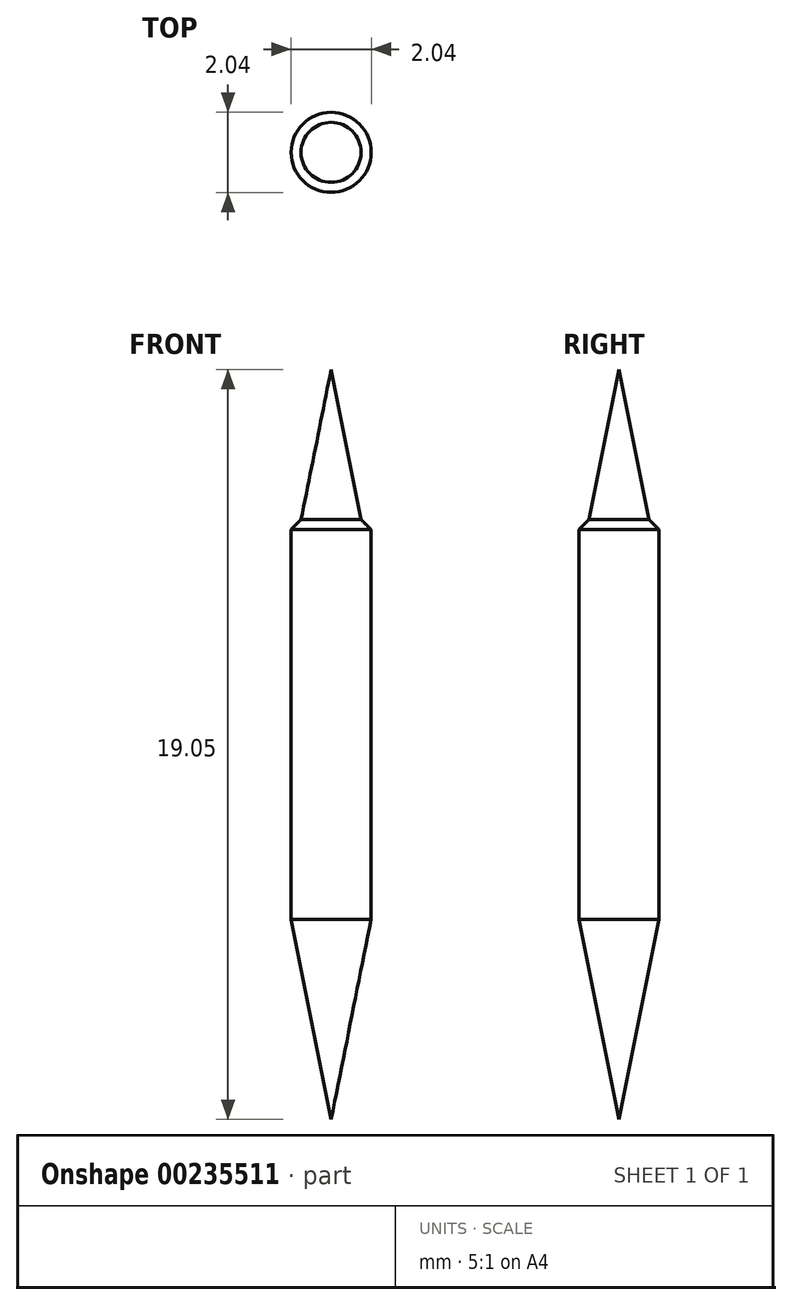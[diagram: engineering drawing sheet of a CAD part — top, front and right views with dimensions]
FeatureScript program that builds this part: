
annotation { "Feature Type Name" : "Feature", "Feature Type Description" : "" }
export const myFeature = defineFeature(function(context is Context, id is Id, definition is map)
    precondition{}
    {
        {
            var Q0;
            Q0=qCreatedBy(makeId("Front.planeOp"),FACE);
            var sketch = newSketch(context, id + "F0", { "sketchPlane" : qUnion([Q0])});
            skLineSegment(sketch, "E0", {"start": v(-1.02, 9.9) * mm, "end": v(-1.02, 0) * mm});
            skLineSegment(sketch, "E1", {"start": v(-1.02, 0) * mm, "end": v(1.02, 0) * mm});
            skLineSegment(sketch, "E2", {"start": v(1.02, 0) * mm, "end": v(1.02, 9.9) * mm});
            skLineSegment(sketch, "E3", {"start": v(1.02, 10.16) * mm, "end": v(-1.02, 10.16) * mm});
            skLineSegment(sketch, "E4", {"start": v(-1.02, 0) * mm, "end": v(0, -5.08) * mm});
            skPoint(sketch, "E4.endSnap0", {"position": v(0, 0) * mm});
            skLineSegment(sketch, "E5", {"start": v(0, -5.08) * mm, "end": v(1.02, 0) * mm});
            skLineSegment(sketch, "E6", {"start": v(-0.76, 10.16) * mm, "end": v(0, 13.97) * mm});
            skLineSegment(sketch, "E7", {"start": v(0, 13.97) * mm, "end": v(0.76, 10.16) * mm});
            skLineSegment(sketch, "E8", {"start": v(-0.76, 10.16) * mm, "end": v(-1.02, 9.9) * mm});
            skLineSegment(sketch, "E9.MirrorCS", {"start": v(0.76, 10.16) * mm, "end": v(1.02, 9.9) * mm});
            skLineSegment(sketch, "E10", {"start": v(-1.02, 9.9) * mm, "end": v(-1.02, 9.9) * mm});
            skLineSegment(sketch, "E11", {"start": v(1.02, 9.9) * mm, "end": v(1.02, 9.9) * mm});
            skLineSegment(sketch, "E12", {"start": v(0, 15.64) * mm, "end": v(0, -6.39) * mm});
            skSolve(sketch);
        }
        {
            var Q0;
            {var subQ4=sQuery(id+"F0.wireOp",EDGE,"E2");Q0=makeQuery(id+"F0.imprint","IMPRINT",FACE,{"disambiguationData":[TD([[makeQuery(id+"F0.imprint","IMPRINT",EDGE,{"derivedFrom":subQ4}),1.0]])]});}
            var Q1;
            {var subQ0=sQuery(id+"F0.wireOp",EDGE,"E7");Q1=makeQuery(id+"F0.imprint","IMPRINT",FACE,{"disambiguationData":[TD([[makeQuery(id+"F0.imprint","IMPRINT",EDGE,{"derivedFrom":subQ0}),-1.0]])]});}
            var Q2;
            {var subQ0=sQuery(id+"F0.wireOp",EDGE,"E5");Q2=makeQuery(id+"F0.imprint","IMPRINT",FACE,{"disambiguationData":[TD([[makeQuery(id+"F0.imprint","IMPRINT",EDGE,{"derivedFrom":subQ0}),1.0]])]});}
            var Q3;
            Q3=sQuery(id+"F0.wireOp",EDGE,"E12");
            revolve(context, id + "F1", {"entities" : qUnion([Q0, Q1, Q2]), "axis" : qUnion([Q3]), "revolveType" : RevolveType.FULL});
        }
    });
